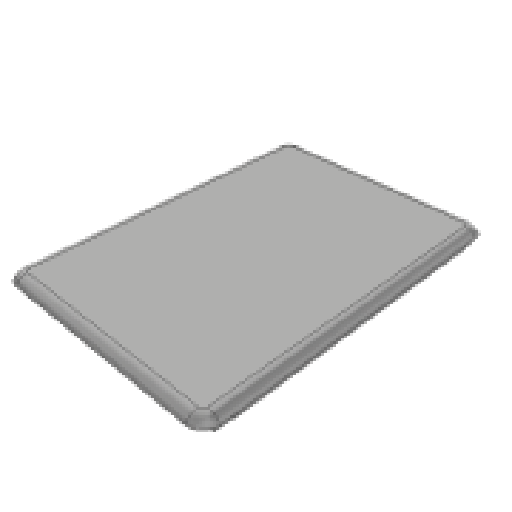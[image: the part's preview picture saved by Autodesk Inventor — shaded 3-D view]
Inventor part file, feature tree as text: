
AUTODESK INVENTOR PART (.ipt)
format: ipt  version: 2025 (Build 290162000, 162)  size: 156,672 bytes
history: native  units: mm
features: extrude x4, sketch x4, reference x4, fillet x3, other x3, projected_geometry x1
ambient origin geometry x8: Origin, YZ Plane, XZ Plane, XY Plane, X Axis, Y Axis, Z Axis, Center Point
bodies: Solid1 (feature_tree)
feature tree (19):
  extrude  "Extrusion1"  Depth=7.6835mm TaperAngle=0.0deg
  fillet  "Fillet1"  Radius=12.7mm
  extrude  "Extrusion2"  Depth=300.0mm TaperAngle=0.0deg
  extrude  "Extrusion3"  Depth=3.175mm
  fillet  "Fillet2"  Radius=17.78mm
  fillet  "Fillet3"  Radius=17.78mm
  extrude  "Extrusion4"  Depth=27.94mm
  sketch  "Sketch1"  dims[d0=330.2mm d1=234.95mm d2=15.875mm d3=7.6835mm d4=0.0mm d5=12.7mm]
  sketch  "Sketch2"  dims[d6=12.7mm d7=0.0mm d8=300.0mm d9=0.0mm]
  reference  "Reference1"
  reference  "Reference2"
  sketch  "Sketch4"  dims[d10=12.7mm d11=3.175mm d12=17.78mm d13=17.78mm]
  reference  "Reference3"
  reference  "Reference4"
  sketch  "Sketch5"  dims[d14=25.4mm d15=27.94mm d16=0.254mm d17=0.0mm]
  projected_geometry  "Projected Loop1"
  other  "<userpath>\Desktop\puppycat\singleSwingarmV2.iam"
  other  "singleSwingarmV2.iam"
  other  "dellLatitudeBase:1"
